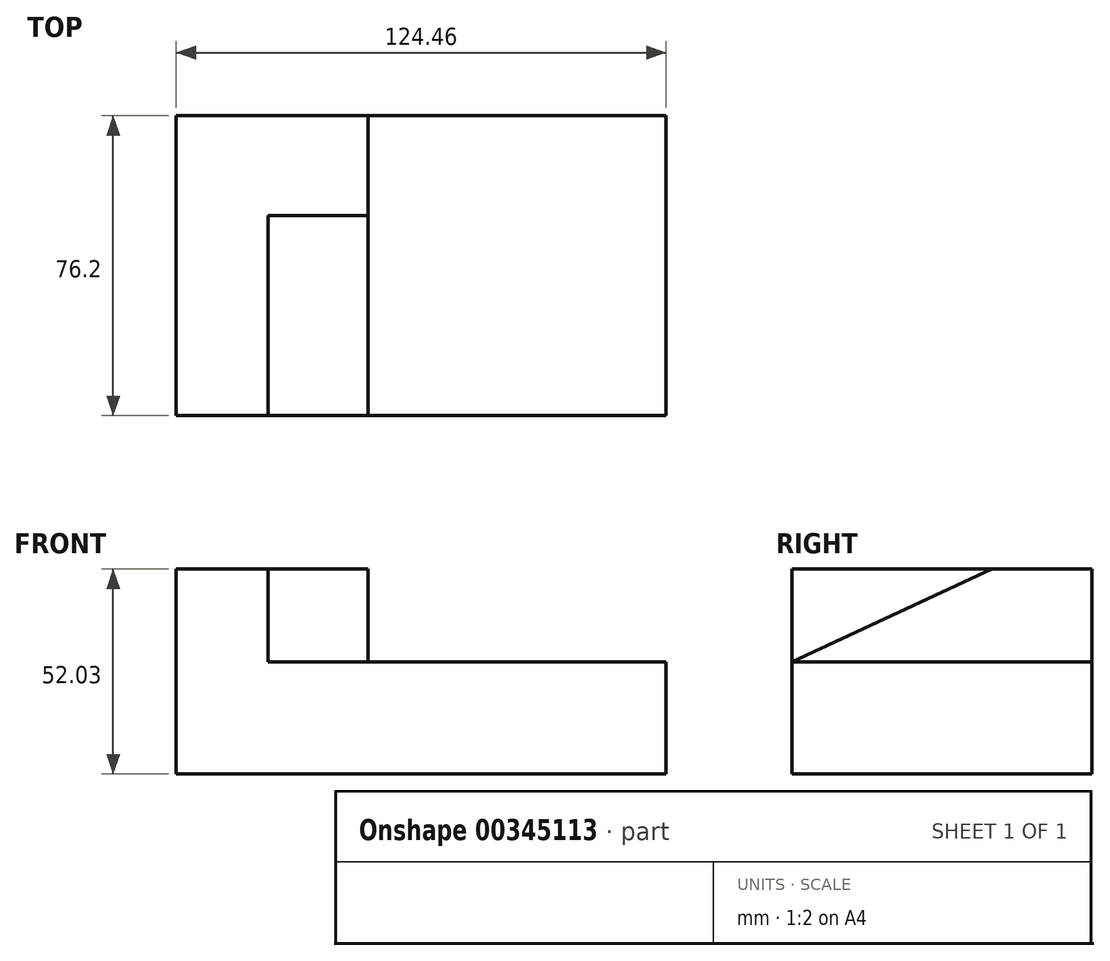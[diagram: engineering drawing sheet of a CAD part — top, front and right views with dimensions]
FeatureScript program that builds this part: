
annotation { "Feature Type Name" : "Feature", "Feature Type Description" : "" }
export const myFeature = defineFeature(function(context is Context, id is Id, definition is map)
    precondition{}
    {
        {
            var Q0;
            Q0=qCreatedBy(makeId("Front.planeOp"),FACE);
            var sketch = newSketch(context, id + "F0", { "sketchPlane" : qUnion([Q0])});
            skLineSegment(sketch, "E0", {"start": v(0, 0) * mm, "end": v(0, 52.03) * mm});
            skLineSegment(sketch, "E1", {"start": v(0, 52.03) * mm, "end": v(48.68, 52.03) * mm});
            skLineSegment(sketch, "E2", {"start": v(48.68, 52.03) * mm, "end": v(48.68, 28.42) * mm});
            skLineSegment(sketch, "E3", {"start": v(48.68, 28.42) * mm, "end": v(124.46, 28.42) * mm});
            skLineSegment(sketch, "E4", {"start": v(124.46, 28.42) * mm, "end": v(124.46, 0) * mm});
            skLineSegment(sketch, "E5", {"start": v(124.46, 0) * mm, "end": v(0, 0) * mm});
            skSolve(sketch);
        }
        {
            var Q0;
            Q0=makeQuery(id+"F0.imprint","IMPRINT",FACE,{"disambiguationData":[TD([[makeQuery(id+"F0.imprint","IMPRINT",EDGE,{"derivedFrom":sQuery(id+"F0.wireOp",EDGE,"E0")}),-1.0]])]});
            extrude(context, id + "F1", {"entities" : qUnion([Q0]), "depth" : 76.2 * mm});
        }
        {
            var Q0;
            Q0=makeQuery(id+"F1.opExtrude","SWEPT_FACE",FACE,{"disambiguationData":[OSD([sQuery(id+"F0.wireOp",EDGE,"E2")])]});
            var sketch = newSketch(context, id + "F2", { "sketchPlane" : qUnion([Q0])});
            skLineSegment(sketch, "E6", {"start": v(-25.4, 52.03) * mm, "end": v(-76.2, 28.42) * mm});
            skLineSegment(sketch, "E7", {"start": v(-76.2, 28.42) * mm, "end": v(-76.2, 52.03) * mm});
            skLineSegment(sketch, "E8", {"start": v(-76.2, 52.03) * mm, "end": v(-25.4, 52.03) * mm});
            skSolve(sketch);
        }
        {
            var Q0;
            Q0=makeQuery(id+"F2.imprint","IMPRINT",FACE,{"disambiguationData":[TD([[makeQuery(id+"F2.imprint","IMPRINT",EDGE,{"derivedFrom":sQuery(id+"F2.wireOp",EDGE,"E6")}),-1.0]])]});
            extrude(context, id + "F3", {"entities" : qUnion([Q0]), "operationType" : NewBodyOperationType.REMOVE, "oppositeDirection" : true, "depth" : 25.4 * mm});
        }
    });
